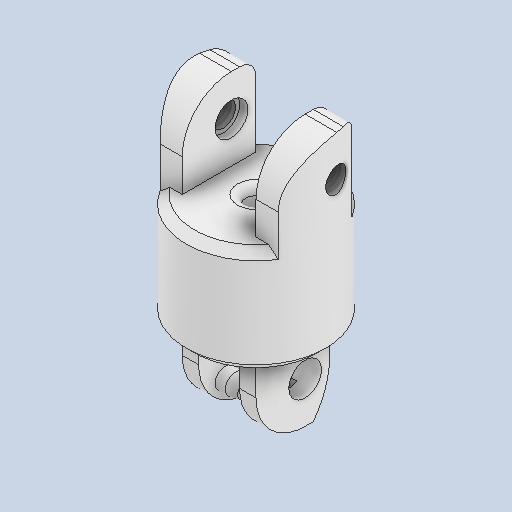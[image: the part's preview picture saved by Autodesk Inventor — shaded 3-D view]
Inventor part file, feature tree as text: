
AUTODESK INVENTOR PART (.ipt)
format: ipt  version: 2022 (Build 260153000, 153)  size: 272,384 bytes
history: native  units: in
note: dims shown in document units (in); Inventor stores cm internally (conversion verified against a paired STEP export)
features: sketch x10, extrude x7, fillet x6, chamfer x4, hole x3, thread x2
ambient origin geometry x8: Origin, YZ Plane, XZ Plane, XY Plane, X Axis, Y Axis, Z Axis, Center Point
bodies: Solid1 (feature_tree)
feature tree (32):
  extrude  "Extrusion1"  Depth=0.3937in
  extrude  "Extrusion2"  Depth=0.0394in TaperAngle=0.0deg
  fillet  "Fillet4"  Radius=0.0394in
  fillet  "Fillet5"  Radius=0.2362in
  fillet  "Fillet6"  Radius=0.3937in
  hole  "Hole1"  [1 undecoded]
  extrude  "Extrusion3"  Depth=0.0492in TaperAngle=0.0deg
  chamfer  "Chamfer1"  Distance=0.0492in Angle=45.0deg
  extrude  "Extrusion4"  Depth=0.0394in TaperAngle=0.0deg
  chamfer  "Chamfer2"  Distance=0.3937in
  extrude  "Extrusion5"  Depth=0.0787in
  fillet  "Fillet8"  Radius=0.1969in
  fillet  "Fillet9"  Radius=0.1969in
  chamfer  "Chamfer3"  Distance=0.0394in Angle=45.0deg
  hole  "Hole2"  [1 undecoded]
  hole  "Hole3"  [1 undecoded]
  chamfer  "Chamfer4"  Distance=0.2362in
  fillet  "Fillet10"  [1 undecoded]
  thread  "Thread1"  [1 undecoded]
  thread  "Thread2"  [1 undecoded]
  sketch  "Sketch1"  dims[d8=0.3937in d9=0.0in d11=0.6693in]
  sketch  "Sketch2"  dims[d12=0.0984in d13=0.0394in d14=0.0in d19=0.0394in d22=0.2362in d23=0.3937in]
  sketch  "Sketch3"  dims[d24=0.1969in]
  sketch  "Sketch4"  dims[d25=0.1575in d26=0.2362in d27=0.1575in d28=0.0787in d29=90.0deg d30=0.3937in d31=0.0in d36=0.0984in d37=0.0in]
  sketch  "Sketch5"  dims[d38=0.0098in d39=0.0492in d40=45.0deg d41=0.0984in d42=0.0in d43=0.0098in d44=0.0492in d45=45.0deg]
  sketch  "Sketch6"  dims[d46=0.4331in d47=0.0in d48=0.0984in d49=0.6693in d51=0.0in d52=0.0394in d55=0.0in d56=0.3937in]
  sketch  "Sketch9"  dims[d63=0.1181in d64=0.2362in d65=0.1575in d66=0.0394in d67=90.0deg d68=0.1575in d69=0.0in d70=0.1969in]
  sketch  "Sketch10"  dims[d71=0.1181in d72=0.2362in d73=0.1575in d74=0.0394in d75=90.0deg d76=0.1575in d77=0.0in d78=0.0394in d79=0.0787in d80=45.0deg d81=0.0394in d82=0.2362in d83=0.0in d84=0.2362in d85=0.0in]
  sketch  "Sketch7"  dims[d57=0.2362in d58=0.0787in]
  sketch  "Sketch8"  dims[d59=0.0394in d60=0.0787in d61=45.0deg d62=0.1969in]
  extrude  "Extrusion6"  [1 undecoded]
  extrude  "Extrusion7"  [1 undecoded]
note: 8 required parameter values undecoded (feature->parameter linkage not recoverable at this tier; creation-order binding heuristic only, values carry confidence <= 0.55)
